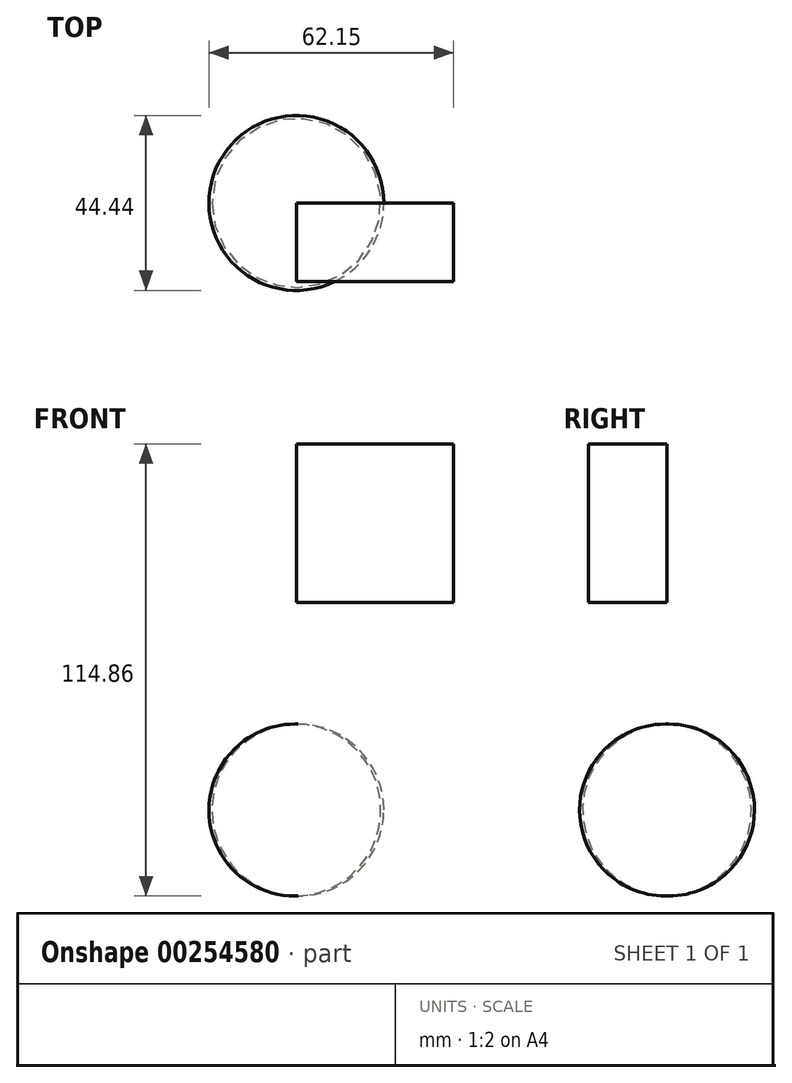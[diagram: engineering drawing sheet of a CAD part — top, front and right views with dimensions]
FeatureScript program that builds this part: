
annotation { "Feature Type Name" : "Feature", "Feature Type Description" : "" }
export const myFeature = defineFeature(function(context is Context, id is Id, definition is map)
    precondition{}
    {
        {
            var Q0;
            Q0=qCreatedBy(makeId("Front.planeOp"),FACE);
            var sketch = newSketch(context, id + "F0", { "sketchPlane" : qUnion([Q0])});
            skLineSegment(sketch, "E0", {"start": v(0, 40.33) * mm, "end": v(39.93, 40.33) * mm});
            skLineSegment(sketch, "E1", {"start": v(39.93, 40.33) * mm, "end": v(39.93, 0) * mm});
            skLineSegment(sketch, "E2", {"start": v(39.93, 0) * mm, "end": v(0, 0) * mm});
            skLineSegment(sketch, "E3", {"start": v(0, 0) * mm, "end": v(0, 40.33) * mm});
            skSolve(sketch);
        }
        {
            var Q0;
            Q0=makeQuery(id+"F0.imprint","IMPRINT",FACE,{"disambiguationData":[TD([[makeQuery(id+"F0.imprint","IMPRINT",EDGE,{"derivedFrom":sQuery(id+"F0.wireOp",EDGE,"E0")}),-1.0]])]});
            extrude(context, id + "F1", {"entities" : qUnion([Q0]), "depth" : 20 * mm});
        }
        {
            var Q0;
            Q0=qCreatedBy(makeId("Front.planeOp"),FACE);
            var sketch = newSketch(context, id + "F2", { "sketchPlane" : qUnion([Q0])});
            skLineSegment(sketch, "E4", {"start": v(0, -30.86) * mm, "end": v(0, -74.52) * mm});
            skArc(sketch, "E5", {"start": v(0, -74.52) * mm, "mid": v(22.22, -52.69) * mm, "end": v(0, -30.86) * mm});
            skSolve(sketch);
        }
        {
            var Q0;
            Q0=makeQuery(id+"F2.imprint","IMPRINT",FACE,{"disambiguationData":[TD([[makeQuery(id+"F2.imprint","IMPRINT",EDGE,{"derivedFrom":sQuery(id+"F2.wireOp",EDGE,"E4")}),1.0]])]});
            var Q1;
            Q1=sQuery(id+"F2.wireOp",EDGE,"E4");
            revolve(context, id + "F3", {"entities" : qUnion([Q0]), "axis" : qUnion([Q1]), "revolveType" : RevolveType.FULL});
        }
    });
